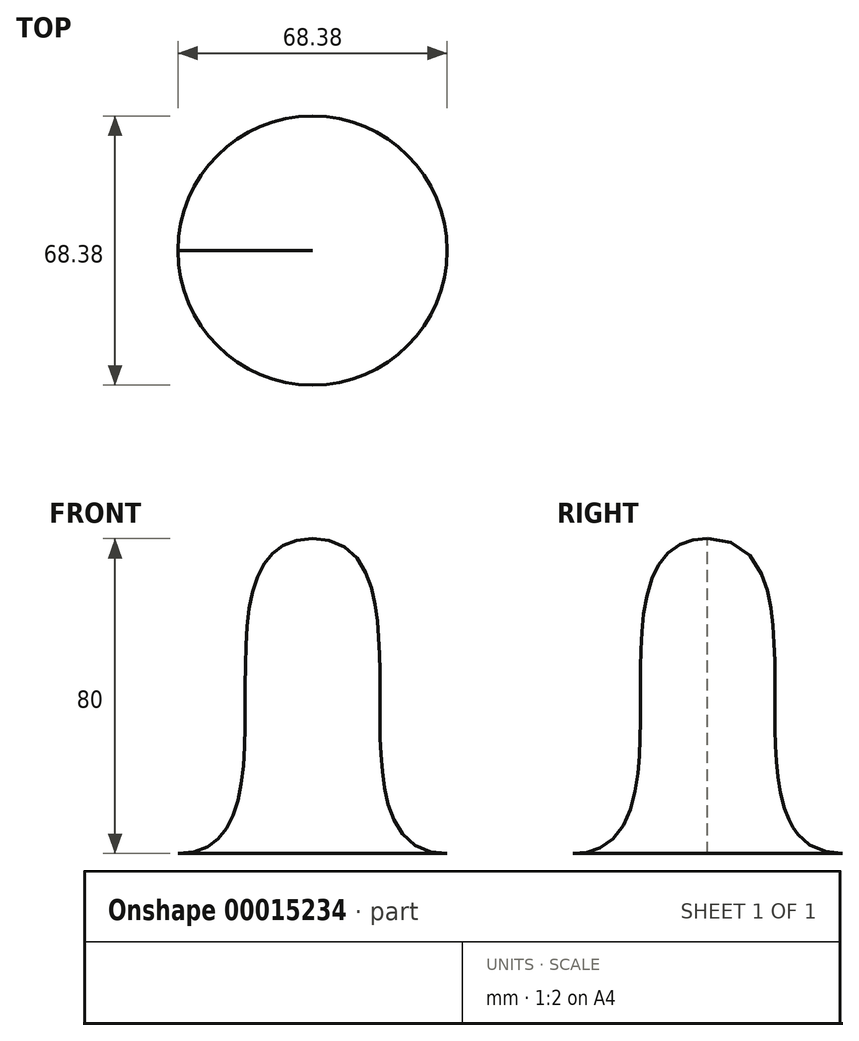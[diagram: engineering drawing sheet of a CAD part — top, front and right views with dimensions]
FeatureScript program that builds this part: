
annotation { "Feature Type Name" : "Feature", "Feature Type Description" : "" }
export const myFeature = defineFeature(function(context is Context, id is Id, definition is map)
    precondition{}
    {
        {
            var Q0;
            Q0=qCreatedBy(makeId("Top.planeOp"),FACE);
            var sketch = newSketch(context, id + "F0", { "sketchPlane" : qUnion([Q0])});
            skCircle(sketch, "E0", {"center": v(0, 0) * mm, "radius": 34.2 * mm});
            skSolve(sketch);
        }
        {
            var Q0;
            Q0=qCreatedBy(makeId("Top.planeOp"),FACE);
            cPlane(context, id + "F1", {"entities" : qUnion([Q0]), "cplaneType" : CPlaneType.OFFSET, "offset" : 80 * mm, "width" : 150 * mm, "height" : 150 * mm});
        }
        {
            var Q0;
            Q0=qCreatedBy(id+"F1.planeOp",FACE);
            var sketch = newSketch(context, id + "F2", { "sketchPlane" : qUnion([Q0])});
            skPoint(sketch, "E1", {"position": v(0, 0) * mm});
            skSolve(sketch);
        }
        {
            var Q0;
            Q0=makeQuery(id+"F0.imprint","IMPRINT",FACE,{"disambiguationData":[TD([[makeQuery(id+"F0.imprint","IMPRINT",EDGE,{"derivedFrom":sQuery(id+"F0.wireOp",EDGE,"E0")}),1.0]])]});
            var Q1;
            Q1=sQuery(id+"F2.wireOp",VERTEX,"E1");
            loft(context, id + "F3", {"startCondition" : LoftEndDerivativeType.TANGENT_TO_PROFILE, "startMagnitude" : 3, "endCondition" : LoftEndDerivativeType.TANGENT_TO_PROFILE, "endMagnitude" : 3, "sheetProfilesArray" : [{ "sheetProfileEntities" : qUnion([Q0]) }, { "sheetProfileEntities" : qUnion([Q1]) }]});
        }
    });
